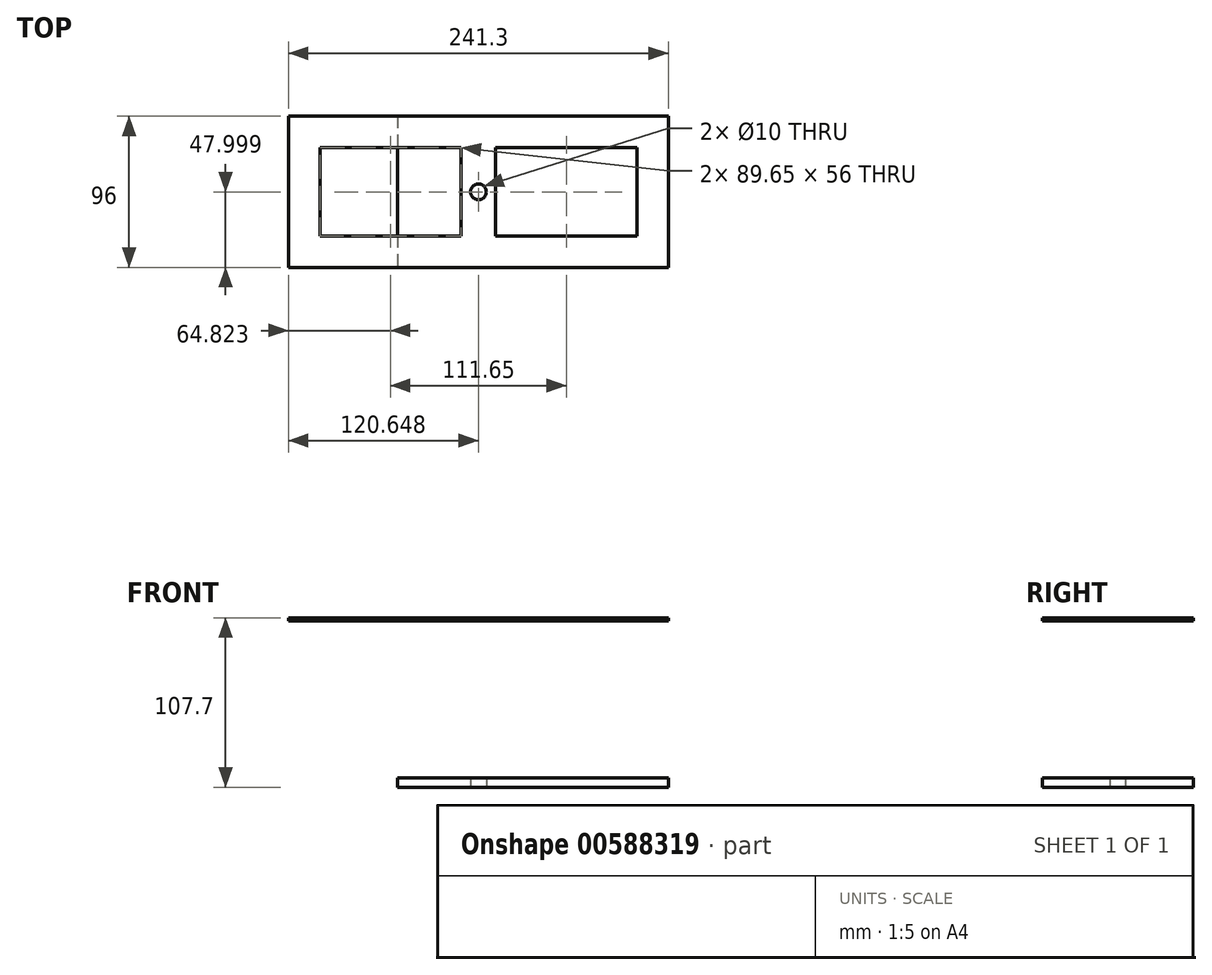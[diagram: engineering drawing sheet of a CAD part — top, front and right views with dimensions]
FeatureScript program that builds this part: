
annotation { "Feature Type Name" : "Feature", "Feature Type Description" : "" }
export const myFeature = defineFeature(function(context is Context, id is Id, definition is map)
    precondition{}
    {
        {
            var Q0;
            Q0=qCreatedBy(makeId("Top.planeOp"),FACE);
            var sketch = newSketch(context, id + "F0", { "sketchPlane" : qUnion([Q0])});
            skLineSegment(sketch, "E0.bottom", {"start": v(-175.94, 50.34) * mm, "end": v(65.36, 50.34) * mm});
            skLineSegment(sketch, "E0.top", {"start": v(-175.94, -45.66) * mm, "end": v(65.36, -45.66) * mm});
            skLineSegment(sketch, "E0.right", {"start": v(65.36, 50.34) * mm, "end": v(65.36, -45.66) * mm});
            skLineSegment(sketch, "E1", {"start": v(65.36, 50.34) * mm, "end": v(-106.6, 50.34) * mm});
            skLineSegment(sketch, "E2", {"start": v(-106.6, 50.34) * mm, "end": v(-106.6, -45.66) * mm});
            skLineSegment(sketch, "E3", {"start": v(65.36, 2.34) * mm, "end": v(-55.3, 2.34) * mm});
            skCircle(sketch, "E4", {"center": v(-55.3, 2.34) * mm, "radius": 5 * mm});
            skSolve(sketch);
        }
        {
            var Q0;
            {var subQ0=sQuery(id+"F0.wireOp",EDGE,"E0.right");Q0=makeQuery(id+"F0.imprint","IMPRINT",FACE,{"disambiguationData":[TD([[makeQuery(id+"F0.imprint","IMPRINT",EDGE,{"derivedFrom":subQ0}),-1.0]])]});}
            extrude(context, id + "F1", {"entities" : qUnion([Q0]), "depth" : 6 * mm, "offsetDistance" : 25 * mm});
        }
        {
            var Q0;
            Q0=makeQuery(id+"F1.opExtrude","SWEPT_FACE",FACE,{"disambiguationData":[OSD([sQuery(id+"F0.wireOp",EDGE,"E0.right")])]});
            var sketch = newSketch(context, id + "F2", { "sketchPlane" : qUnion([Q0])});
            skLineSegment(sketch, "E5", {"start": v(50.34, 0) * mm, "end": v(50.34, 107.7) * mm});
            skLineSegment(sketch, "E6", {"start": v(50.34, 107.7) * mm, "end": v(-45.66, 107.7) * mm});
            skLineSegment(sketch, "E7", {"start": v(-45.66, 107.7) * mm, "end": v(-45.66, 0) * mm});
            skLineSegment(sketch, "E8", {"start": v(50.34, 107.7) * mm, "end": v(50.34, 105.7) * mm});
            skLineSegment(sketch, "E9", {"start": v(50.34, 105.7) * mm, "end": v(-45.66, 105.7) * mm});
            skSolve(sketch);
        }
        {
            var Q0;
            {var subQ0=sQuery(id+"F2.wireOp",EDGE,"E6");Q0=makeQuery(id+"F2.imprint","IMPRINT",FACE,{"disambiguationData":[TD([[makeQuery(id+"F2.imprint","IMPRINT",EDGE,{"derivedFrom":subQ0}),1.0]])]});}
            extrude(context, id + "F3", {"entities" : qUnion([Q0]), "oppositeDirection" : true, "depth" : 241.3 * mm, "offsetDistance" : 25 * mm});
        }
        {
            var Q0;
            Q0=makeQuery(id+"F3.opExtrude","SWEPT_FACE",FACE,{"disambiguationData":[OSD([sQuery(id+"F2.wireOp",EDGE,"E6")])]});
            var sketch = newSketch(context, id + "F4", { "sketchPlane" : qUnion([Q0])});
            skLineSegment(sketch, "E10.0", {"start": v(-155.94, 30.34) * mm, "end": v(-65.3, 30.34) * mm});
            skLineSegment(sketch, "E10.1", {"start": v(-155.94, 30.34) * mm, "end": v(-155.94, -25.66) * mm});
            skLineSegment(sketch, "E10.2", {"start": v(-155.94, -25.66) * mm, "end": v(-65.3, -25.66) * mm});
            skLineSegment(sketch, "E10.3", {"start": v(45.36, 30.34) * mm, "end": v(45.36, -25.66) * mm});
            skPoint(sketch, "E11.end.orphan", {"position": v(-55.3, 30.34) * mm});
            skPoint(sketch, "E12.start.orphan", {"position": v(-55.3, 2.34) * mm});
            skLineSegment(sketch, "E13.trimOffspring", {"start": v(-45.3, 30.34) * mm, "end": v(45.36, 30.34) * mm});
            skLineSegment(sketch, "E14.trimOffspring", {"start": v(-45.3, -25.66) * mm, "end": v(45.36, -25.66) * mm});
            skPoint(sketch, "E15.start.orphan", {"position": v(-55.3, -25.66) * mm});
            skCircle(sketch, "E16", {"center": v(-55.3, 2.34) * mm, "radius": 5 * mm});
            skLineSegment(sketch, "E17", {"start": v(-45.3, 30.34) * mm, "end": v(-44.3, 30.34) * mm});
            skLineSegment(sketch, "E18", {"start": v(-44.3, 30.34) * mm, "end": v(-44.3, -25.66) * mm});
            skPoint(sketch, "E19.endSnap0", {"position": v(-44.3, 2.34) * mm});
            skLineSegment(sketch, "E20", {"start": v(-66.3, 2.34) * mm, "end": v(-66.3, -25.66) * mm});
            skLineSegment(sketch, "E21", {"start": v(-66.3, 2.34) * mm, "end": v(-66.3, 30.34) * mm});
            skSolve(sketch);
        }
        {
            var Q0;
            Q0=makeQuery(id+"F4.imprint","IMPRINT",FACE,{"disambiguationData":[TD([[makeQuery(id+"F4.imprint","IMPRINT",EDGE,{"derivedFrom":sQuery(id+"F4.wireOp",EDGE,"E10.0")}),-1.0]])]});
            extrude(context, id + "F5", {"entities" : qUnion([Q0]), "operationType" : NewBodyOperationType.REMOVE, "oppositeDirection" : true, "depth" : 25 * mm, "offsetDistance" : 25 * mm});
        }
        {
            var Q0;
            Q0=makeQuery(id+"F4.imprint","IMPRINT",FACE,{"disambiguationData":[TD([[makeQuery(id+"F4.imprint","IMPRINT",EDGE,{"derivedFrom":sQuery(id+"F4.wireOp",EDGE,"E10.3")}),-1.0]])]});
            var Q1;
            Q1=makeQuery(id+"F4.imprint","IMPRINT",FACE,{"disambiguationData":[TD([[makeQuery(id+"F4.imprint","IMPRINT",EDGE,{"derivedFrom":sQuery(id+"F4.wireOp",EDGE,"E16")}),1.0]])]});
            extrude(context, id + "F6", {"entities" : qUnion([Q0, Q1]), "operationType" : NewBodyOperationType.REMOVE, "oppositeDirection" : true, "depth" : 25 * mm, "offsetDistance" : 25 * mm});
        }
    });
